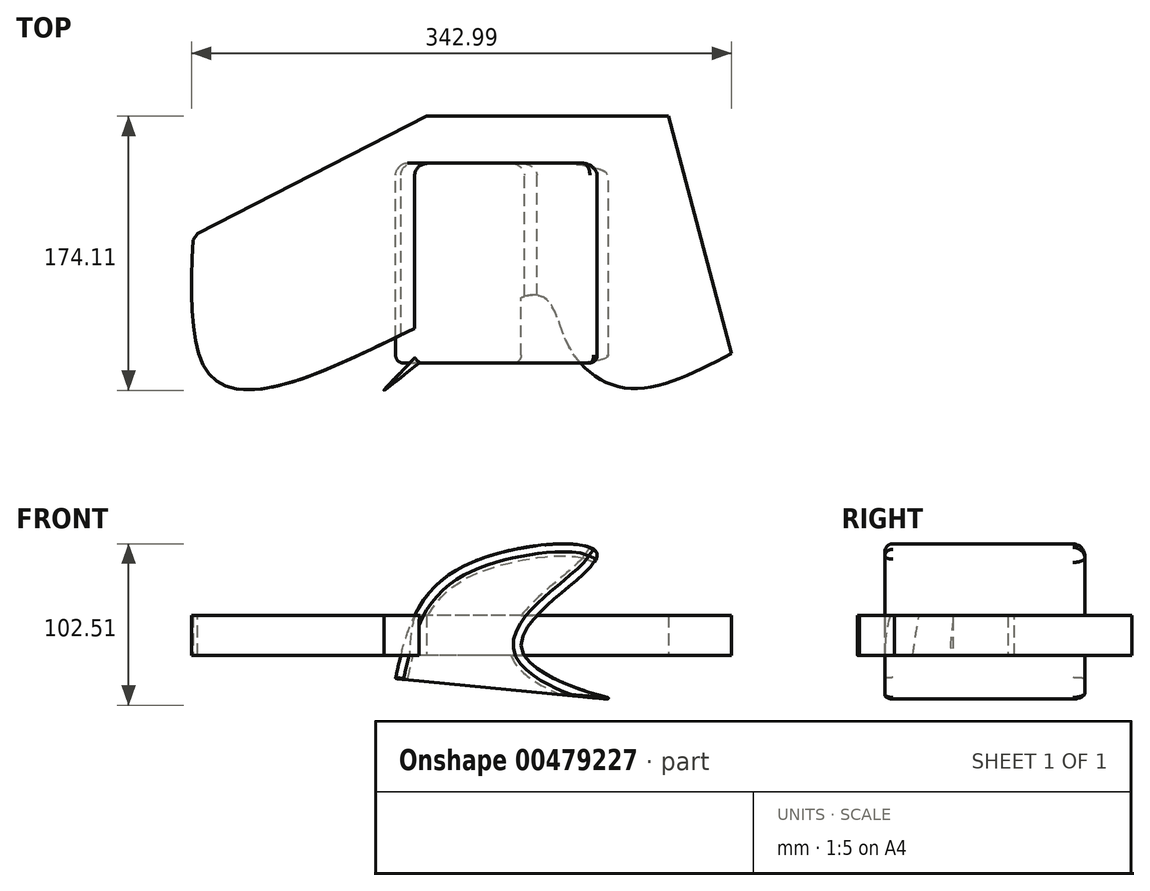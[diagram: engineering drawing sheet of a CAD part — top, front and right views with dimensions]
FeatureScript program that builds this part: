
annotation { "Feature Type Name" : "Feature", "Feature Type Description" : "" }
export const myFeature = defineFeature(function(context is Context, id is Id, definition is map)
    precondition{}
    {
        {
            var Q0;
            Q0=qCreatedBy(makeId("Front.planeOp"),FACE);
            var sketch = newSketch(context, id + "F0", { "sketchPlane" : qUnion([Q0])});
            skFitSpline(sketch, "E0", {"points": [v(-53.74, -14.65) * mm, v(-11.3, 56.25) * mm, v(74.36, 63.27) * mm, v(26.39, 4.07) * mm, v(97.82, -29.67) * mm, v(97.82, -29.15) * mm], "startDerivative": vector(76.75, 341.29) * mm, "endDerivative": vector(-19.41, 31.06) * mm});
            skLineSegment(sketch, "E1", {"start": v(-53.74, -14.65) * mm, "end": v(97.95, -29.35) * mm});
            skSolve(sketch);
        }
        {
            var Q0;
            {var subQ0=sQuery(id+"F0.wireOp",EDGE,"E1");var subQ1=sQuery(id+"F0.wireOp",EDGE,"E0");var subQ2=makeQuery(id+"F0.imprint","INTERSECT",VERTEX,{"disambiguationData":[OD(0.0)],"derivedFrom":[subQ1,subQ0]});Q0=makeQuery(id+"F0.imprint","IMPRINT",FACE,{"disambiguationData":[TD([[makeQuery(id+"F0.imprint","IMPRINT",EDGE,{"disambiguationData":[TD([[subQ2,-1.0]])],"derivedFrom":subQ1}),-1.0]])]});}
            extrude(context, id + "F1", {"entities" : qUnion([Q0]), "endBound" : BoundingType.SYMMETRIC, "depth" : 127 * mm});
        }
        {
            var Q0;
            Q0=makeQuery(id+"F1.opExtrude","CAP_EDGE",EDGE,{"disambiguationData":[OSD([sQuery(id+"F0.wireOp",EDGE,"E0")])],"isStart":true});
            fillet(context, id + "F2", {"entities" : qUnion([Q0]), "radius" : 7.62 * mm, "tangentPropagation" : true, "allowEdgeOverflow" : false});
        }
        {
            var Q0;
            Q0=makeQuery(id+"F1.opExtrude","CAP_EDGE",EDGE,{"disambiguationData":[OSD([sQuery(id+"F0.wireOp",EDGE,"E0")])],"isStart":false});
            fillet(context, id + "F3", {"entities" : qUnion([Q0]), "radius" : 5.08 * mm, "tangentPropagation" : true, "allowEdgeOverflow" : false});
        }
        {
            var Q0;
            {var subQ0=sQuery(id+"F0.wireOp",EDGE,"E1");var subQ1=sQuery(id+"F0.wireOp",EDGE,"E0");Q0=makeQuery(id+"F1.opExtrude","SWEPT_EDGE",EDGE,{"disambiguationData":[OSD([subQ1,subQ0]),TDD([makeQuery(id+"F0.imprint","INTERSECT",VERTEX,{"disambiguationData":[OD(2.0)],"derivedFrom":[subQ1,subQ0]})])]});}
            fillet(context, id + "F4", {"entities" : qUnion([Q0]), "radius" : 0.5 * mm, "tangentPropagation" : true, "allowEdgeOverflow" : false});
        }
        {
            var Q0;
            Q0=qCreatedBy(makeId("Top.planeOp"),FACE);
            var sketch = newSketch(context, id + "F5", { "sketchPlane" : qUnion([Q0])});
            skFitSpline(sketch, "E2", {"points": [v(159.8, -57.46) * mm, v(93.26, -79.29) * mm, v(55.05, -50.26) * mm, v(32.28, -20.3) * mm, v(-61.07, -80.71) * mm, v(-23.8, -38.35) * mm, v(-97.42, -67.46) * mm, v(-170.6, -72.13) * mm, v(-182.2, 17.56) * mm], "startDerivative": vector(-554.54, -285.23) * mm, "endDerivative": vector(33.25, 782.07) * mm});
            skLineSegment(sketch, "E3", {"start": v(159.8, -57.46) * mm, "end": v(119.69, 93.35) * mm});
            skLineSegment(sketch, "E4", {"start": v(119.69, 93.35) * mm, "end": v(-33.9, 93.35) * mm});
            skLineSegment(sketch, "E5", {"start": v(-33.9, 93.35) * mm, "end": v(-182.2, 17.56) * mm});
            skSolve(sketch);
        }
        {
            var Q0;
            Q0 = qSketchRegion(id + "F5", true);
            extrude(context, id + "F6", {"entities" : qUnion([Q0]), "operationType" : NewBodyOperationType.ADD, "depth" : 25.4 * mm});
        }
        {
            var Q0;
            Q0=makeQuery(id+"F6.opExtrude","SWEPT_EDGE",EDGE,{"disambiguationData":[OSD([sQuery(id+"F5.wireOp",EDGE,"E2"),sQuery(id+"F5.wireOp",EDGE,"E5")])]});
            chamfer(context, id + "F7", {"entities" : qUnion([Q0]), "width" : 5.08 * mm, "tangentPropagation" : true});
        }
    });
